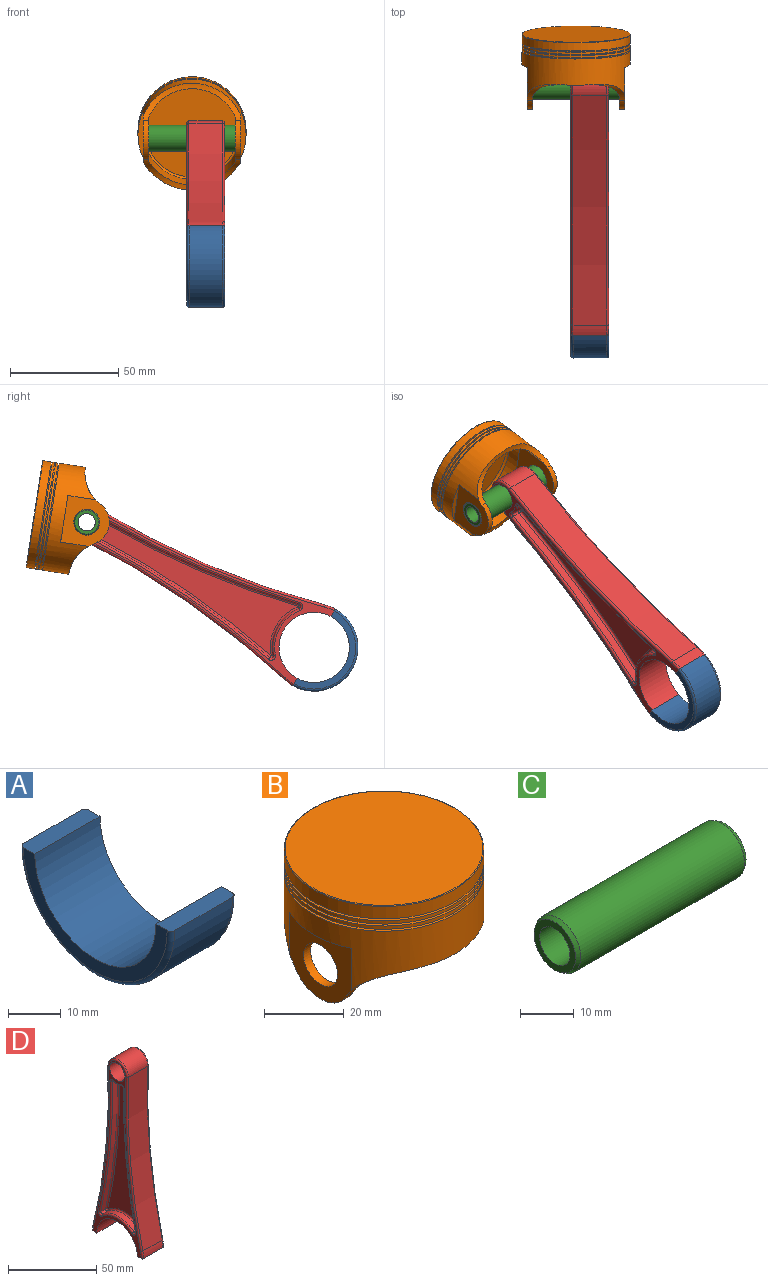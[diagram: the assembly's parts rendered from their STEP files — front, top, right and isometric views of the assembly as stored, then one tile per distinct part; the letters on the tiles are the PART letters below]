
ASSEMBLY  parts=4 mates=3
PART A: 8 faces, bbox 17.5x43.8x21.9 mm
  f0: plane 17.5x4mm, normal (0,0,1), area 69.6mm2, adj f1,f2,f3,f4,f5,f6
  f1: torus R=19.25mm, axis (-1,0,0), area 98.1mm2, adj f0,f2,f5,f7
  f2: plane 38.5x19.25mm, normal (-1,0,0), area 167.3mm2, adj f0,f1,f3,f7
  f3: cylinder r=16.25mm len=32.5mm, axis (-1,0,0), area 893.4mm2, adj f0,f2,f6,f7
  f4: torus R=19.25mm, axis (1,0,0), area 98.1mm2, adj f0,f5,f6,f7
  f5: cylinder r=20.25mm len=40.5mm, axis (-1,0,0), area 986.1mm2, adj f0,f1,f4,f7
  f6: plane 38.5x19.25mm, normal (1,0,0), area 167.3mm2, adj f0,f3,f4,f7
  f7: plane 17.5x4mm, normal (0,0,1), area 69.6mm2, adj f1,f2,f3,f4,f5,f6
PART B: 32 faces, bbox 54.1x54.1x35 mm
  f0: cylinder r=25mm len=50mm, axis (0,0,1), area 1794.2mm2, adj f1,f2,f3,f4,f8,f9,f18
  f1: plane 21.79x21mm, normal (1,0,0), area 292.4mm2, adj f0,f3,f7,f8,f9,f10
  f2: plane 21.79x21mm, normal (-1,0,0), area 292.4mm2, adj f0,f4,f5,f6,f8,f9
  f3: plane 21.79x2.5mm, normal (0,0,-1), area 36.7mm2, adj f0,f1
  f4: plane 21.79x2.5mm, normal (0,0,-1), area 36.7mm2, adj f0,f2
  f5: cylinder r=6mm len=12mm, axis (1,0,0), area 94.2mm2, adj f2,f14
  f6: cylinder r=10.5mm len=18.53mm, axis (1,0,0), area 56.7mm2, adj f2,f8,f9,f14
  f7: cylinder r=10.5mm len=18.53mm, axis (1,0,0), area 56.7mm2, adj f1,f8,f9,f15
  f8: cylinder r=17.83mm len=45mm, axis (1,0,0), area 159.3mm2, adj f0,f1,f2,f6,f7,f14,f15,f16
  f9: cylinder r=17.83mm len=45mm, axis (1,0,0), area 159.2mm2, adj f0,f1,f2,f6,f7,f14,f15,f16
  f10: cylinder r=6mm len=12mm, axis (1,0,0), area 94.2mm2, adj f1,f15
  f11: plane 43x43mm, normal (0,0,-1), area 1452.2mm2, adj f31
  f12: plane 20.62x2.5mm, normal (0,0,1), area 34.8mm2, adj f15,f16
  f13: plane 20.62x2.5mm, normal (0,0,1), area 34.8mm2, adj f14,f16
  f14: plane 23.5x20.62mm, normal (1,0,0), area 328.3mm2, adj f5,f6,f8,f9,f13,f16
  f15: plane 23.5x20.62mm, normal (-1,0,0), area 328.3mm2, adj f7,f8,f9,f10,f12,f16
  f16: cylinder r=22.5mm len=45mm, axis (0,0,1), area 2151.9mm2, adj f8,f9,f12,f13,f14,f15,f31
  f17: plane 50x50mm, normal (0,0,-1), area 153.9mm2, adj f19,f20
  f18: plane 50x50mm, normal (0,0,1), area 153.9mm2, adj f0,f19
  f19: cylinder r=24mm len=48mm, axis (0,0,-1), area 90.5mm2, adj f17,f18
  f20: cylinder r=25mm len=50mm, axis (0,0,1), area 157.1mm2, adj f17,f22
  f21: plane 50x50mm, normal (0,0,-1), area 153.9mm2, adj f23,f24
  f22: plane 50x50mm, normal (0,0,1), area 153.9mm2, adj f20,f23
  f23: cylinder r=24mm len=48mm, axis (0,0,-1), area 90.5mm2, adj f21,f22
  f24: cylinder r=25mm len=50mm, axis (0,0,1), area 157.1mm2, adj f21,f26
  f25: plane 50x50mm, normal (0,0,-1), area 153.9mm2, adj f27,f29
  f26: plane 50x50mm, normal (0,0,1), area 153.9mm2, adj f24,f27
  f27: cylinder r=24mm len=48mm, axis (0,0,-1), area 90.5mm2, adj f25,f26
  f28: plane 49.6x49.6mm, normal (0,0,1), area 1932.2mm2, adj f30
  f29: cylinder r=25mm len=50mm, axis (0,0,1), area 596.9mm2, adj f25,f30
  f30: torus R=24.8mm, axis (0,0,1), area 49.2mm2, adj f28,f29
  f31: torus R=21.5mm, axis (0,0,1), area 218.5mm2, adj f11,f16
PART C: 6 faces, bbox 45x12x12 mm
  f0: cylinder r=4mm len=45mm, axis (-1,0,0), area 1131mm2, adj f2,f3
  f1: cylinder r=6mm len=43.27mm, axis (-1,0,0), area 1631.2mm2, adj f4,f5
  f2: plane 11x11mm, normal (1,0,0), area 44.8mm2, adj f0,f5
  f3: plane 11x11mm, normal (-1,0,0), area 44.8mm2, adj f0,f4
  f4: cone r=6mm half-angle=30deg, axis (1,0,0), area 36.1mm2, adj f1,f3
  f5: cone r=5.5mm half-angle=30deg, axis (-1,0,0), area 36.1mm2, adj f1,f2
PART D: 71 faces, bbox 17.5x40.8x128.7 mm
  f0: cylinder r=20.25mm len=15.5mm, axis (-1,0,0), area 77.2mm2, adj f2,f6,f36,f70
  f1: torus R=19.25mm, axis (1,0,0), area 7.7mm2, adj f3,f5,f38,f69
  f2: torus R=19.25mm, axis (-1,0,0), area 7.7mm2, adj f0,f39,f65,f70
  f3: plane 127x38.5mm, normal (1,0,0), area 425.9mm2, adj f1,f7,f9,f20,f25,f26,f29,f30
  f4: cylinder r=400mm len=114.72mm, axis (-1,0,0), area 1793.6mm2, adj f5,f8,f38,f68
  f5: cylinder r=20.25mm len=15.5mm, axis (-1,0,0), area 77.2mm2, adj f1,f4,f66,f69
  f6: cylinder r=400mm len=114.72mm, axis (-1,0,0), area 1793.6mm2, adj f0,f8,f35,f65
  f7: cylinder r=6mm len=17.5mm, axis (-1,0,0), area 659.7mm2, adj f3,f39
  f8: cylinder r=8mm len=16mm, axis (-1,0,0), area 400.3mm2, adj f4,f6,f37,f67
  f9: cylinder r=16.25mm len=32.5mm, axis (-1,0,0), area 893.4mm2, adj f3,f39,f69,f70
  f10: cylinder r=403mm len=94.99mm, axis (-1,0,0), area 358.8mm2, adj f15,f19,f20,f21
  f11: cylinder r=403mm len=94.99mm, axis (-1,0,0), area 358.8mm2, adj f23,f28,f31,f34
  f12: cylinder r=9mm len=6.67mm, axis (-1,0,0), area 25.6mm2, adj f18,f19,f28,f29
  f13: cylinder r=19.25mm len=24.81mm, axis (-1,0,0), area 101.1mm2, adj f21,f22,f30,f31
  f14: plane 95.22x26.09mm, normal (1,0,0), area 1143.5mm2, adj f15,f18,f22,f23
  f15: torus R=404mm, axis (1,0,0), area 150.4mm2, adj f10,f14,f16,f17
  f16: sphere r=1mm, area 2mm2, adj f15,f18,f19
  f17: sphere r=1mm, area 2.5mm2, adj f15,f21,f22
  f18: torus R=10mm, axis (1,0,0), area 11.2mm2, adj f12,f14,f16,f24
  f19: cylinder r=1mm len=3.75mm, axis (1,0,0), area 7.4mm2, adj f10,f12,f16,f25
  f20: torus R=402mm, axis (1,0,0), area 150.1mm2, adj f3,f10,f25,f26
  f21: cylinder r=1mm len=3.75mm, axis (1,0,0), area 9.3mm2, adj f10,f13,f17,f26
  f22: torus R=20.25mm, axis (1,0,0), area 43.1mm2, adj f13,f14,f17,f27
  f23: torus R=404mm, axis (1,0,0), area 150.4mm2, adj f11,f14,f24,f27
  f24: sphere r=1mm, area 2mm2, adj f18,f23,f28
  f25: torus R=2mm, axis (1,0,0), area 4.2mm2, adj f3,f19,f20,f29
  f26: torus R=2mm, axis (1,0,0), area 5.3mm2, adj f3,f20,f21,f30
  f27: sphere r=1mm, area 2.5mm2, adj f22,f23,f31
  f28: cylinder r=1mm len=3.75mm, axis (1,0,0), area 7.4mm2, adj f11,f12,f24,f32
  f29: torus R=8mm, axis (1,0,0), area 10.3mm2, adj f3,f12,f25,f32
  f30: torus R=18.25mm, axis (1,0,0), area 41.5mm2, adj f3,f13,f26,f33
  f31: cylinder r=1mm len=3.75mm, axis (1,0,0), area 9.3mm2, adj f11,f13,f27,f33
  f32: torus R=2mm, axis (1,0,0), area 4.2mm2, adj f3,f28,f29,f34
  f33: torus R=2mm, axis (1,0,0), area 5.3mm2, adj f3,f30,f31,f34
  f34: torus R=402mm, axis (1,0,0), area 150.1mm2, adj f3,f11,f32,f33
  f35: torus R=401mm, axis (1,0,0), area 181.9mm2, adj f3,f6,f36,f37
  f36: torus R=19.25mm, axis (1,0,0), area 7.7mm2, adj f0,f3,f35,f70
  f37: torus R=7mm, axis (1,0,0), area 38.7mm2, adj f3,f8,f35,f38
  f38: torus R=401mm, axis (1,0,0), area 181.9mm2, adj f1,f3,f4,f37
  f39: plane 127x38.5mm, normal (-1,0,0), area 425.9mm2, adj f2,f7,f9,f50,f55,f56,f59,f60
  f40: cylinder r=403mm len=94.99mm, axis (1,0,0), area 358.8mm2, adj f45,f49,f50,f51
  f41: cylinder r=403mm len=94.99mm, axis (1,0,0), area 358.8mm2, adj f53,f58,f61,f64
  f42: cylinder r=9mm len=6.67mm, axis (1,0,0), area 25.6mm2, adj f48,f49,f58,f59
  f43: cylinder r=19.25mm len=24.81mm, axis (1,0,0), area 101.1mm2, adj f51,f52,f60,f61
  f44: plane 95.22x26.09mm, normal (-1,0,0), area 1143.5mm2, adj f45,f48,f52,f53
  f45: torus R=404mm, axis (-1,0,0), area 150.4mm2, adj f40,f44,f46,f47
  f46: sphere r=1mm, area 2mm2, adj f45,f48,f49
  f47: sphere r=1mm, area 2.5mm2, adj f45,f51,f52
  f48: torus R=10mm, axis (-1,0,0), area 11.2mm2, adj f42,f44,f46,f54
  f49: cylinder r=1mm len=3.75mm, axis (-1,0,0), area 7.4mm2, adj f40,f42,f46,f55
  f50: torus R=402mm, axis (-1,0,0), area 150.1mm2, adj f39,f40,f55,f56
  f51: cylinder r=1mm len=3.75mm, axis (-1,0,0), area 9.3mm2, adj f40,f43,f47,f56
  f52: torus R=20.25mm, axis (-1,0,0), area 43.1mm2, adj f43,f44,f47,f57
  f53: torus R=404mm, axis (-1,0,0), area 150.4mm2, adj f41,f44,f54,f57
  f54: sphere r=1mm, area 2mm2, adj f48,f53,f58
  f55: torus R=2mm, axis (-1,0,0), area 4.2mm2, adj f39,f49,f50,f59
  f56: torus R=2mm, axis (-1,0,0), area 5.3mm2, adj f39,f50,f51,f60
  f57: sphere r=1mm, area 2.5mm2, adj f52,f53,f61
  f58: cylinder r=1mm len=3.75mm, axis (-1,0,0), area 7.4mm2, adj f41,f42,f54,f62
  f59: torus R=8mm, axis (-1,0,0), area 10.3mm2, adj f39,f42,f55,f62
  f60: torus R=18.25mm, axis (-1,0,0), area 41.5mm2, adj f39,f43,f56,f63
  f61: cylinder r=1mm len=3.75mm, axis (-1,0,0), area 9.3mm2, adj f41,f43,f57,f63
  f62: torus R=2mm, axis (-1,0,0), area 4.2mm2, adj f39,f58,f59,f64
  f63: torus R=2mm, axis (-1,0,0), area 5.3mm2, adj f39,f60,f61,f64
  f64: torus R=402mm, axis (-1,0,0), area 150.1mm2, adj f39,f41,f62,f63
  f65: torus R=401mm, axis (-1,0,0), area 181.9mm2, adj f2,f6,f39,f67
  f66: torus R=19.25mm, axis (-1,0,0), area 7.7mm2, adj f5,f39,f68,f69
  f67: torus R=7mm, axis (-1,0,0), area 38.7mm2, adj f8,f39,f65,f68
  f68: torus R=401mm, axis (-1,0,0), area 181.9mm2, adj f4,f39,f66,f67
  f69: plane 17.5x4mm, normal (0,0,-1), area 69.6mm2, adj f1,f3,f5,f9,f39,f66
  f70: plane 17.5x4mm, normal (0,0,-1), area 69.6mm2, adj f0,f2,f3,f9,f36,f39
PLACE A rot(axis=(-1,0,0),61.2deg) t=(-36.93,-97.21,139.34)mm
PLACE B rot(axis=(-1,0,0),81.2deg) t=(-43.24,-73.01,143.09)mm
PLACE C rot(axis=(-1,0,0),81.2deg) t=(-43.23,-97.22,139.34)mm
PLACE D rot(axis=(-1,0,0),61.2deg) t=(-36.93,-97.21,139.34)mm
MATE fastened B.f5 <-> C.f1  axis (-1,0,0) through (-65.73,-97.23,139.33)mm
MATE fastened D.f69 <-> A.f7  axis (0,-0.88,-0.48) through (-36.87,-211.14,97.47)mm
MATE cylindrical D.f8 <-> C.f1  axis (-1,0,0) through (-36.93,-97.21,139.34)mm
